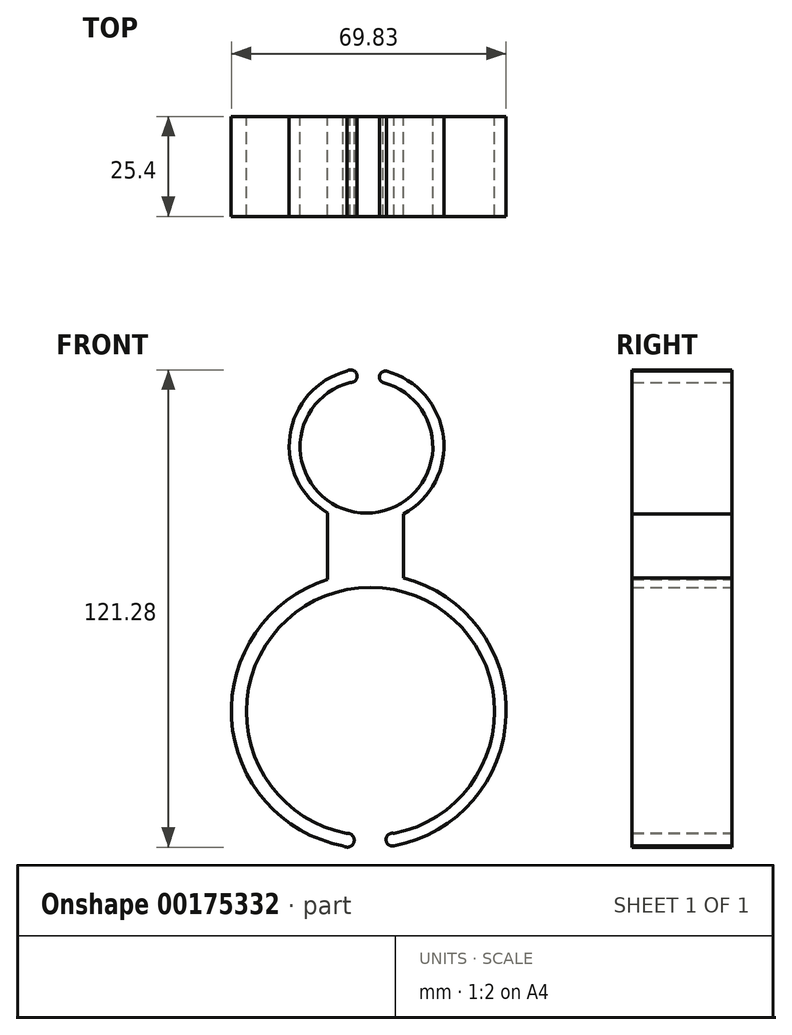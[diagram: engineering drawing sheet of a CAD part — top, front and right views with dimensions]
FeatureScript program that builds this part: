
annotation { "Feature Type Name" : "Feature", "Feature Type Description" : "" }
export const myFeature = defineFeature(function(context is Context, id is Id, definition is map)
    precondition{}
    {
        {
            var Q0;
            Q0=qCreatedBy(makeId("Front.planeOp"),FACE);
            var sketch = newSketch(context, id + "F0", { "sketchPlane" : qUnion([Q0])});
            skArc(sketch, "E0", {"start": v(-5.43, 52.39) * mm, "mid": v(-0.42, 13.72) * mm, "end": v(4.64, 52.38) * mm});
            skArc(sketch, "E1", {"start": v(-4.6, 49.5) * mm, "mid": v(-0.43, 16.33) * mm, "end": v(3.74, 49.5) * mm});
            skLineSegment(sketch, "E2", {"start": v(-10.35, 16.42) * mm, "end": v(-10.35, 0) * mm});
            skLineSegment(sketch, "E3", {"start": v(8.97, 16.1) * mm, "end": v(8.97, 0) * mm});
            skArc(sketch, "E4", {"start": v(6.62, -68.2) * mm, "mid": v(0.14, 1.02) * mm, "end": v(-6.33, -68.2) * mm});
            skArc(sketch, "E5", {"start": v(6.62, -65.04) * mm, "mid": v(0.58, -2.58) * mm, "end": v(-5.47, -65.04) * mm});
            skArc(sketch, "E6", {"start": v(-4.6, 49.5) * mm, "mid": v(-2.87, 51.56) * mm, "end": v(-5.43, 52.39) * mm});
            skArc(sketch, "E7", {"start": v(4.64, 52.38) * mm, "mid": v(2.93, 51.34) * mm, "end": v(3.74, 49.5) * mm});
            skArc(sketch, "E8", {"start": v(-6.33, -68.2) * mm, "mid": v(-3.59, -67.26) * mm, "end": v(-5.47, -65.04) * mm});
            skArc(sketch, "E9", {"start": v(6.62, -65.04) * mm, "mid": v(4.55, -66.63) * mm, "end": v(6.62, -68.2) * mm});
            skLineSegment(sketch, "E10", {"start": v(8.97, 0) * mm, "end": v(8.97, -0.11) * mm});
            skLineSegment(sketch, "E11", {"start": v(-10.35, 0) * mm, "end": v(-10.35, -0.6) * mm});
            skSolve(sketch);
        }
        {
            var Q0;
            Q0=makeQuery(id+"F0.imprint","IMPRINT",FACE,{"disambiguationData":[TD([[makeQuery(id+"F0.imprint","IMPRINT",EDGE,{"derivedFrom":sQuery(id+"F0.wireOp",EDGE,"E1")}),-1.0]])]});
            var Q1;
            {var subQ4=sQuery(id+"F0.wireOp",EDGE,"E2");Q1=makeQuery(id+"F0.imprint","IMPRINT",FACE,{"disambiguationData":[TD([[makeQuery(id+"F0.imprint","IMPRINT",EDGE,{"derivedFrom":subQ4}),1.0]])]});}
            var Q2;
            Q2=makeQuery(id+"F0.imprint","IMPRINT",FACE,{"disambiguationData":[TD([[makeQuery(id+"F0.imprint","IMPRINT",EDGE,{"derivedFrom":sQuery(id+"F0.wireOp",EDGE,"E5")}),-1.0]])]});
            extrude(context, id + "F1", {"entities" : qUnion([Q0, Q1, Q2]), "depth" : 25.4 * mm});
        }
    });
